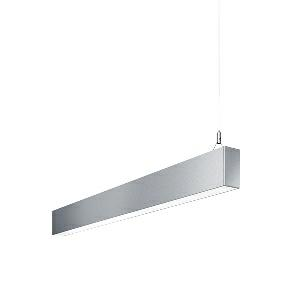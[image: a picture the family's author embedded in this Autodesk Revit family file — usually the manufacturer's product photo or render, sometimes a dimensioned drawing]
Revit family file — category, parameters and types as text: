
# Revit family: dotoo_line_-_dlp_2000_830_d_end_00805850_c5e7
name_source: partatom
category: Lighting Fixtures
units: mm (PartAtom-declared; Revit-internal decimal feet)

## family parameters
Cut with Voids When Loaded = No
Host = Face
Light Source = No
Part Type = Normal
Room Calculation Point = No
Round Connector Dimension = Use Diameter
Shared = No

## types (1)
- DOTOO.line - DLP 2000/830/D END (1 x LED, 1650 lm, 3000K)
    Apparent Load = 16 VA
    Approval mark = CE
    CIE Flux Codes = 67 91 98 100 100
    Color Rendering = 80-89
    Color Temperature = 3000K
    Control Gear = Electronic ballast
    Default Elevation = 1800 mm
    Description = DLP 2000/830/D|Suspended luminaire|light source: LED|connected load: 220-240 V, 50/60 Hz|Power consumption: approx. 16 W|standby: approx. 0,15|luminous flux: 1650 lm|luminous efficacy: 103 lm/W|light distribution: Direct|direct ratio: approx. 100 %|colour temperature: Warm white, ca. 3000 K|color rendering index (CRI): >= 80|chromaticity tolerance:  3 SDCM|System of protection: IP40|technology: DALI, Continuously dimmable|luminaire body|material: Sectional aluminium|colour: silver|lamp cover: acrylic clear|mains lead: 1,0 m With free stranded wires|Fastening: Steel cable 0.3 - 0.7 m|glare control: Conical prismatic screen|luminance(L65): <= 3000 cd/m|unified glare rating(4H 8H): <= 19|special features: DALI Load 1x, TouchDIM - dimming via standard switch, Through-wired, up to 18 m on one mains connection, Flicker-free, Suitable as emergency lighting, Mechanical and electrical connection of the individual modules without tools|
    Frequency = 50 Hz
    Height = 110 mm
    Lamp = 1 x LED
    Lamp Light Flux = 1650 lm
    Lamp count = 1
    Length = 1408 mm
    Luminous efficacy = 103 lm/W
    Manufacturer = Waldmann
    ModVariant = No
    Model = 00805850
    Mounting Place = Ceiling
    Mounting Type = Pendant
    Number of Poles = 1
    OnlyDefault = Yes
    Power Factor = 1
    Product Name = DOTOO.line - DLP 2000/830/D END
    Product group = Suspended luminaire
    ProductGroupID = 9
    Protection Class = Protection class I
    Protection Degree = IP 40
    RLX_Detail_Level = 1
    RLX_Emergency_Light_Flux = 0 lm
    RLX_Emergency_Type = 0
    RLX_Emergency_Type_DB = No
    RlxData = <blob elided: 20837 chars, md5=06c683cc>
    Socket = socket
    Standby Power = 0 W
    System Light Flux = 1650 lm
    System Power = 16 W
    Type Comments = Product without accessories
    Type Image = 113312000-00692600.jpg
    URL = http://relux.com
    VarID = ---
    Voltage = 230 V
    Voltage Range = 220-240 V
    Weight = 0.00 kg
    Width = 60 mm  [stored 0.19685 ft]

note: [stored X ft] marks values corroborated as IEEE doubles in the binary element streams (Revit-internal decimal feet)

## geometry (parser evidence)
native form markers: Blend x4, Sweep x11
no freeform markers — native parametric forms only
